# Revit family: TD92_ALI038_VER040_RVT20_R00
name_source: partatom
category: Mobiliário
units: mm (PartAtom-declared; Revit-internal decimal feet)

## family parameters
Com base no plano de trabalho = Não
Compartilhado = Não
Corte com vazios quando carregada = Não
Número OmniClass = 23.40.20.00
Ponto de cálculo do ambiente = Não
Sempre na vertical = Sim
Título OmniClass = General Furniture and Specialties

## types (1)
- TD92_ALI038_VER040_RVT20_R00
    Descrição = Cada detalhe da Cadeira Tramontina Alice Satinada Vermelha sem Braços em Polipropileno da linha Summa é surpreedente. Uma cadeira projetada com um design diferenciado, moderno e belo, características que a tornam singular e encantadora. Além disso, a Alice oferece alta durabilidade e conforto para o uso diário. Ela é excelente para compor diversos ambientes, sejam eles residenciais ou comerciais, possibilitando compor facilmente com a decoração do espaço. Produzida em monobloco empilhável, a cadeira é leve e perfeita para áreas internas. Para conservar suas características originais e sua beleza, é aconselhado não subir no assento, jogar-se na cadeira ou apoiar-se somente nas duas pernas traseiras. Evitar longa exposição ao sol. A Alice resiste a uma carga estática de até 182 kg.
    Elevação padrão = 0  [stored 0 ft]
    Fabricante = Tramontina Delta S/A
    Modelo = Cadeira Tramontina Alice Satinada Vermelha sem Braços em Polipropileno
    Nota-chave = 92038040
    URL = https://www.tramontinastore.com

note: [stored X ft] marks values corroborated as IEEE doubles in the binary element streams (Revit-internal decimal feet)
